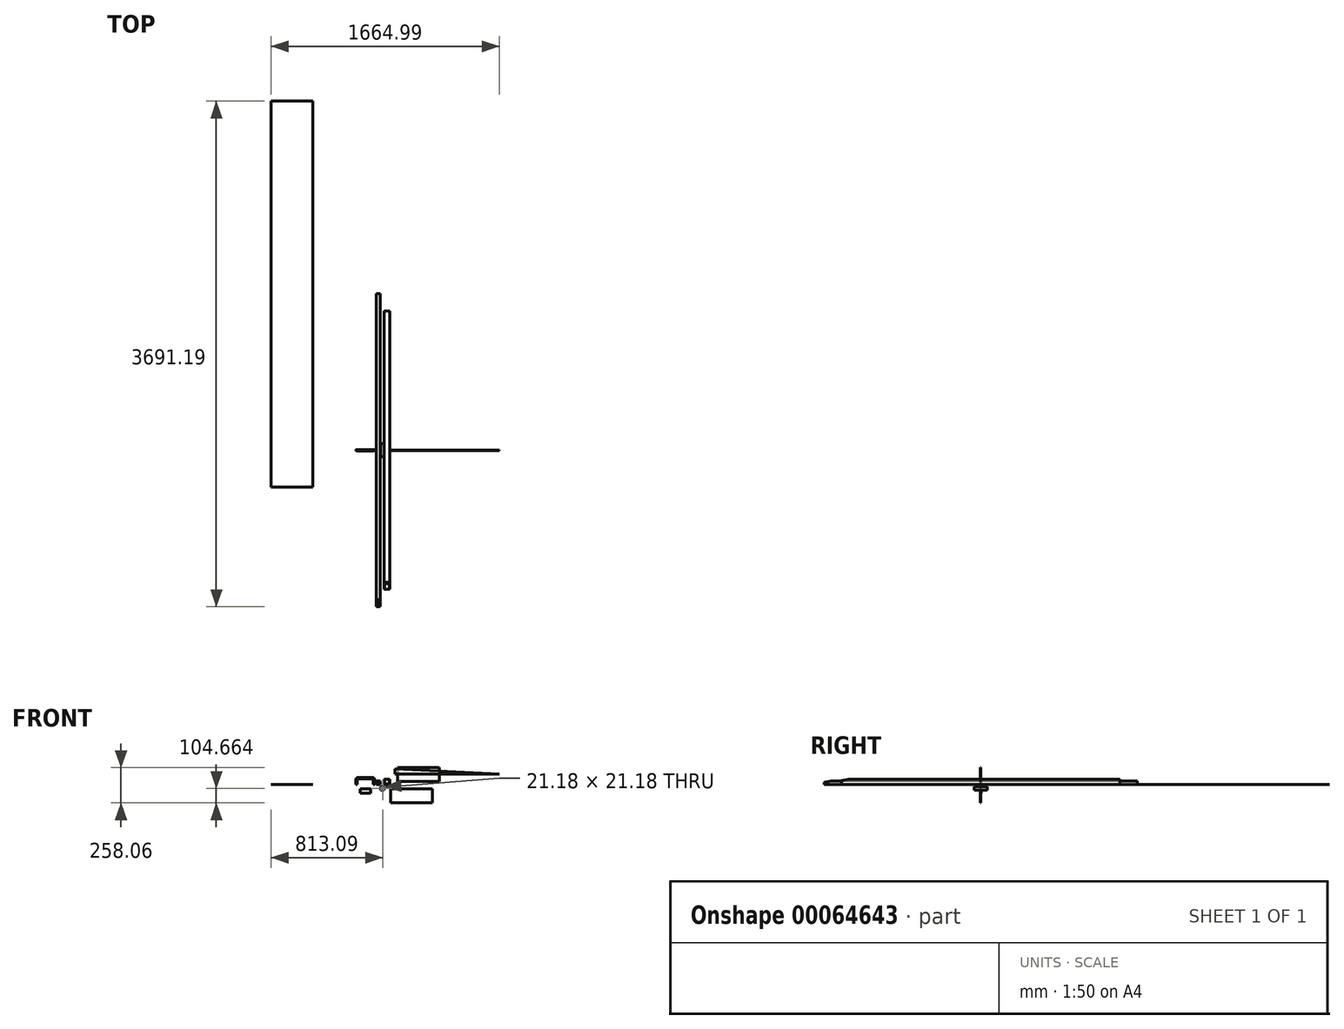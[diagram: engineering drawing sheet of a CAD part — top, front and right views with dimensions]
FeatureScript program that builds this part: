
annotation { "Feature Type Name" : "Feature", "Feature Type Description" : "" }
export const myFeature = defineFeature(function(context is Context, id is Id, definition is map)
    precondition{}
    {
        {
            var Q0;
            Q0=qCreatedBy(makeId("Front.planeOp"),FACE);
            var sketch = newSketch(context, id + "F0", { "sketchPlane" : qUnion([Q0])});
            skLineSegment(sketch, "E0.bottom", {"start": v(0, 0) * mm, "end": v(38.1, 0) * mm});
            skLineSegment(sketch, "E0.top", {"start": v(0, 38.1) * mm, "end": v(38.1, 38.1) * mm});
            skLineSegment(sketch, "E0.left", {"start": v(0, 0) * mm, "end": v(0, 38.1) * mm});
            skLineSegment(sketch, "E0.right", {"start": v(38.1, 0) * mm, "end": v(38.1, 38.1) * mm});
            skLineSegment(sketch, "E1.bottom", {"start": v(1.65, 36.45) * mm, "end": v(36.45, 36.45) * mm});
            skLineSegment(sketch, "E1.top", {"start": v(1.65, 1.65) * mm, "end": v(36.45, 1.65) * mm});
            skLineSegment(sketch, "E1.left", {"start": v(1.65, 36.45) * mm, "end": v(1.65, 1.65) * mm});
            skLineSegment(sketch, "E1.right", {"start": v(36.45, 36.45) * mm, "end": v(36.45, 1.65) * mm});
            skSolve(sketch);
        }
        {
            var Q0;
            Q0=makeQuery(id+"F0.imprint","IMPRINT",FACE,{"disambiguationData":[TD([[makeQuery(id+"F0.imprint","IMPRINT",EDGE,{"derivedFrom":sQuery(id+"F0.wireOp",EDGE,"E0.bottom")}),1.0]])]});
            extrude(context, id + "F1", {"entities" : qUnion([Q0]), "endBound" : BoundingType.SYMMETRIC, "depth" : 2032 * mm});
        }
        {
            var Q0;
            Q0=qCreatedBy(makeId("Front.planeOp"),FACE);
            var sketch = newSketch(context, id + "F2", { "sketchPlane" : qUnion([Q0])});
            skLineSegment(sketch, "E2.bottom", {"start": v(-31.74, 0) * mm, "end": v(-57.14, 0) * mm});
            skLineSegment(sketch, "E2.top", {"start": v(-31.74, 25.4) * mm, "end": v(-57.14, 25.4) * mm});
            skLineSegment(sketch, "E2.left", {"start": v(-31.74, 0) * mm, "end": v(-31.74, 25.4) * mm});
            skLineSegment(sketch, "E2.right", {"start": v(-57.14, 0) * mm, "end": v(-57.14, 25.4) * mm});
            skLineSegment(sketch, "E3.bottom", {"start": v(-55.03, 23.3) * mm, "end": v(-33.85, 23.3) * mm});
            skLineSegment(sketch, "E3.top", {"start": v(-55.03, 2.1) * mm, "end": v(-33.85, 2.1) * mm});
            skLineSegment(sketch, "E3.left", {"start": v(-55.03, 23.3) * mm, "end": v(-55.03, 2.1) * mm});
            skLineSegment(sketch, "E3.right", {"start": v(-33.85, 23.3) * mm, "end": v(-33.85, 2.1) * mm});
            skSolve(sketch);
        }
        {
            var Q0;
            Q0=makeQuery(id+"F2.imprint","IMPRINT",FACE,{"disambiguationData":[TD([[makeQuery(id+"F2.imprint","IMPRINT",EDGE,{"derivedFrom":sQuery(id+"F2.wireOp",EDGE,"E2.bottom")}),-1.0]])]});
            extrude(context, id + "F3", {"entities" : qUnion([Q0]), "endBound" : BoundingType.SYMMETRIC, "depth" : 2286 * mm});
        }
        {
            var Q0;
            Q0=qCreatedBy(makeId("Front.planeOp"),FACE);
            var sketch = newSketch(context, id + "F4", { "sketchPlane" : qUnion([Q0])});
            skLineSegment(sketch, "E4.bottom", {"start": v(-25.4, -17.9) * mm, "end": v(0, -17.9) * mm});
            skLineSegment(sketch, "E4.top", {"start": v(-25.4, -43.3) * mm, "end": v(0, -43.3) * mm});
            skLineSegment(sketch, "E4.left", {"start": v(-25.4, -17.9) * mm, "end": v(-25.4, -43.3) * mm});
            skLineSegment(sketch, "E4.right", {"start": v(0, -17.9) * mm, "end": v(0, -43.3) * mm});
            skLineSegment(sketch, "E5.bottom", {"start": v(-23.3, -20.01) * mm, "end": v(-2.1, -20.01) * mm});
            skLineSegment(sketch, "E5.top", {"start": v(-23.3, -41.2) * mm, "end": v(-2.1, -41.2) * mm});
            skLineSegment(sketch, "E5.left", {"start": v(-23.3, -20.01) * mm, "end": v(-23.3, -41.2) * mm});
            skLineSegment(sketch, "E5.right", {"start": v(-2.1, -20.01) * mm, "end": v(-2.1, -41.2) * mm});
            skSolve(sketch);
        }
        {
            var Q0;
            Q0=makeQuery(id+"F4.imprint","IMPRINT",FACE,{"disambiguationData":[TD([[makeQuery(id+"F4.imprint","IMPRINT",EDGE,{"derivedFrom":sQuery(id+"F4.wireOp",EDGE,"E4.bottom")}),-1.0]])]});
            extrude(context, id + "F5", {"entities" : qUnion([Q0]), "endBound" : BoundingType.SYMMETRIC, "depth" : 95.25 * mm});
        }
        {
            var Q0;
            Q0=qCreatedBy(makeId("Front.planeOp"),FACE);
            var sketch = newSketch(context, id + "F6", { "sketchPlane" : qUnion([Q0])});
            skLineSegment(sketch, "E6.bottom", {"start": v(45.4, -33.67) * mm, "end": v(350.2, -33.67) * mm});
            skLineSegment(sketch, "E6.top", {"start": v(45.4, -135.27) * mm, "end": v(350.2, -135.27) * mm});
            skLineSegment(sketch, "E6.left", {"start": v(45.4, -33.67) * mm, "end": v(45.4, -135.27) * mm});
            skLineSegment(sketch, "E6.right", {"start": v(350.2, -33.67) * mm, "end": v(350.2, -135.27) * mm});
            skSolve(sketch);
        }
        {
            var Q0;
            Q0=makeQuery(id+"F6.imprint","IMPRINT",FACE,{"disambiguationData":[TD([[makeQuery(id+"F6.imprint","IMPRINT",EDGE,{"derivedFrom":sQuery(id+"F6.wireOp",EDGE,"E6.bottom")}),-1.0]])]});
            extrude(context, id + "F7", {"entities" : qUnion([Q0]), "endBound" : BoundingType.SYMMETRIC, "depth" : 3.17 * mm});
        }
        {
            var Q0;
            Q0=qCreatedBy(makeId("Front.planeOp"),FACE);
            var sketch = newSketch(context, id + "F8", { "sketchPlane" : qUnion([Q0])});
            skLineSegment(sketch, "E7.bottom", {"start": v(-175.7, -33.57) * mm, "end": v(-99.5, -33.57) * mm});
            skLineSegment(sketch, "E7.top", {"start": v(-175.7, -65.32) * mm, "end": v(-99.5, -65.32) * mm});
            skLineSegment(sketch, "E7.left", {"start": v(-175.7, -33.57) * mm, "end": v(-175.7, -65.32) * mm});
            skLineSegment(sketch, "E7.right", {"start": v(-99.5, -33.57) * mm, "end": v(-99.5, -65.32) * mm});
            skSolve(sketch);
        }
        {
            var Q0;
            Q0=makeQuery(id+"F8.imprint","IMPRINT",FACE,{"disambiguationData":[TD([[makeQuery(id+"F8.imprint","IMPRINT",EDGE,{"derivedFrom":sQuery(id+"F8.wireOp",EDGE,"E7.bottom")}),-1.0]])]});
            extrude(context, id + "F9", {"entities" : qUnion([Q0]), "endBound" : BoundingType.SYMMETRIC, "depth" : 6.35 * mm});
        }
        {
            var Q0;
            Q0=qCreatedBy(makeId("Front.planeOp"),FACE);
            var sketch = newSketch(context, id + "F10", { "sketchPlane" : qUnion([Q0])});
            skLineSegment(sketch, "E8", {"start": v(-203.2, 0) * mm, "end": v(-203.2, 34.92) * mm});
            skLineSegment(sketch, "E9", {"start": v(-193.68, 44.45) * mm, "end": v(-85.73, 44.45) * mm});
            skLineSegment(sketch, "E10", {"start": v(-76.2, 34.92) * mm, "end": v(-76.2, 0) * mm});
            skPoint(sketch, "E11.visualSharp", {"position": v(-203.2, 44.45) * mm});
            skArc(sketch, "E11.filletArc", {"start": v(-193.68, 44.45) * mm, "mid": v(-200.41, 41.66) * mm, "end": v(-203.2, 34.92) * mm});
            skPoint(sketch, "E12.visualSharp", {"position": v(-76.2, 44.45) * mm});
            skArc(sketch, "E12.filletArc", {"start": v(-76.2, 34.92) * mm, "mid": v(-78.99, 41.66) * mm, "end": v(-85.73, 44.45) * mm});
            skSolve(sketch);
        }
        {
            var Q0;
            Q0=qCreatedBy(makeId("Top.planeOp"),FACE);
            var sketch = newSketch(context, id + "F11", { "sketchPlane" : qUnion([Q0])});
            skCircle(sketch, "E13", {"center": v(-76.2, 0) * mm, "radius": 4.76 * mm});
            skSolve(sketch);
        }
        {
            var Q0;
            Q0 = qSketchRegion(id + "F11", true);
            var Q1;
            Q1 = qConstructionFilter(qBodyType(qCreatedBy(id + "F10" ,EDGE), BodyType.WIRE), ConstructionObject.NO);
            sweep(context, id + "F12", {"profiles" : qUnion([Q0]), "path" : qUnion([Q1])});
        }
        {
            var Q0;
            Q0=qCreatedBy(makeId("Front.planeOp"),FACE);
            var sketch = newSketch(context, id + "F13", { "sketchPlane" : qUnion([Q0])});
            skLineSegment(sketch, "E14.bottom", {"start": v(95.73, 122.8) * mm, "end": v(400.53, 122.8) * mm});
            skLineSegment(sketch, "E14.top", {"start": v(95.73, 21.2) * mm, "end": v(400.53, 21.2) * mm});
            skLineSegment(sketch, "E14.left", {"start": v(95.73, 122.8) * mm, "end": v(95.73, 21.2) * mm});
            skLineSegment(sketch, "E14.right", {"start": v(400.53, 122.8) * mm, "end": v(400.53, 21.2) * mm});
            skSolve(sketch);
        }
        {
            var Q0;
            Q0=makeQuery(id+"F13.imprint","IMPRINT",FACE,{"disambiguationData":[TD([[makeQuery(id+"F13.imprint","IMPRINT",EDGE,{"derivedFrom":sQuery(id+"F13.wireOp",EDGE,"E14.bottom")}),-1.0]])]});
            extrude(context, id + "F14", {"entities" : qUnion([Q0]), "endBound" : BoundingType.SYMMETRIC, "depth" : 1.59 * mm});
        }
        {
            var Q0;
            Q0=qCreatedBy(makeId("Top.planeOp"),FACE);
            var sketch = newSketch(context, id + "F15", { "sketchPlane" : qUnion([Q0])});
            skLineSegment(sketch, "E15.bottom", {"start": v(-825.8, 2548.19) * mm, "end": v(-521, 2548.19) * mm});
            skLineSegment(sketch, "E15.top", {"start": v(-825.8, -271.21) * mm, "end": v(-521, -271.21) * mm});
            skLineSegment(sketch, "E15.left", {"start": v(-825.8, 2548.19) * mm, "end": v(-825.8, -271.21) * mm});
            skLineSegment(sketch, "E15.right", {"start": v(-521, 2548.19) * mm, "end": v(-521, -271.21) * mm});
            skSolve(sketch);
        }
        {
            var Q0;
            Q0=makeQuery(id+"F15.imprint","IMPRINT",FACE,{"disambiguationData":[TD([[makeQuery(id+"F15.imprint","IMPRINT",EDGE,{"derivedFrom":sQuery(id+"F15.wireOp",EDGE,"E15.bottom")}),-1.0]])]});
            extrude(context, id + "F16", {"entities" : qUnion([Q0]), "endBound" : BoundingType.SYMMETRIC, "depth" : 1.78 * mm});
        }
        {
            var Q0;
            Q0=makeQuery(id+"F1.opExtrude","SWEPT_FACE",FACE,{"disambiguationData":[OSD([sQuery(id+"F0.wireOp",EDGE,"E0.right")])]});
            var sketch = newSketch(context, id + "F17", { "sketchPlane" : qUnion([Q0])});
            skLineSegment(sketch, "E16", {"start": v(-1016, 38.1) * mm, "end": v(-1016, 29.14) * mm});
            skLineSegment(sketch, "E17", {"start": v(-1016, 29.14) * mm, "end": v(-965.2, 38.1) * mm});
            skLineSegment(sketch, "E18", {"start": v(-965.2, 38.1) * mm, "end": v(-1016, 38.1) * mm});
            skSolve(sketch);
        }
        {
            var Q0;
            Q0=makeQuery(id+"F17.imprint","IMPRINT",FACE,{"disambiguationData":[TD([[makeQuery(id+"F17.imprint","IMPRINT",EDGE,{"derivedFrom":sQuery(id+"F17.wireOp",EDGE,"E16")}),-1.0]])]});
            var Q1;
            Q1=makeQuery(id+"F1.opExtrude","SWEPT_FACE",FACE,{"disambiguationData":[OSD([sQuery(id+"F0.wireOp",EDGE,"E0.left")])]});
            extrude(context, id + "F18", {"entities" : qUnion([Q0]), "operationType" : NewBodyOperationType.REMOVE, "endBound" : BoundingType.UP_TO_SURFACE, "oppositeDirection" : true, "endBoundEntityFace" : qUnion([Q1]), "depth" : 25.4 * mm});
        }
        {
            var Q0;
            Q0=makeQuery(id+"F3.opExtrude","SWEPT_FACE",FACE,{"disambiguationData":[OSD([sQuery(id+"F2.wireOp",EDGE,"E2.left")])]});
            var sketch = newSketch(context, id + "F19", { "sketchPlane" : qUnion([Q0])});
            skLineSegment(sketch, "E19", {"start": v(-1143, 25.4) * mm, "end": v(-1143, 16.44) * mm});
            skLineSegment(sketch, "E20", {"start": v(-1143, 16.44) * mm, "end": v(-1092.2, 25.4) * mm});
            skLineSegment(sketch, "E21", {"start": v(-1092.2, 25.4) * mm, "end": v(-1143, 25.4) * mm});
            skSolve(sketch);
        }
        {
            var Q0;
            Q0=makeQuery(id+"F19.imprint","IMPRINT",FACE,{"disambiguationData":[TD([[makeQuery(id+"F19.imprint","IMPRINT",EDGE,{"derivedFrom":sQuery(id+"F19.wireOp",EDGE,"E19")}),-1.0]])]});
            var Q1;
            Q1=makeQuery(id+"F3.opExtrude","SWEPT_FACE",FACE,{"disambiguationData":[OSD([sQuery(id+"F2.wireOp",EDGE,"E2.right")])]});
            extrude(context, id + "F20", {"entities" : qUnion([Q0]), "operationType" : NewBodyOperationType.REMOVE, "endBound" : BoundingType.UP_TO_SURFACE, "oppositeDirection" : true, "endBoundEntityFace" : qUnion([Q1]), "depth" : 25.4 * mm});
        }
        {
            var Q0;
            Q0=qCreatedBy(makeId("Front.planeOp"),FACE);
            var sketch = newSketch(context, id + "F21", { "sketchPlane" : qUnion([Q0])});
            skLineSegment(sketch, "E22", {"start": v(77.2, 74.06) * mm, "end": v(77.2, 112.16) * mm});
            skLineSegment(sketch, "E23", {"start": v(77.2, 112.16) * mm, "end": v(839.2, 74.06) * mm});
            skLineSegment(sketch, "E24", {"start": v(839.2, 74.06) * mm, "end": v(77.2, 74.06) * mm});
            skSolve(sketch);
        }
        {
            var Q0;
            Q0=makeQuery(id+"F21.imprint","IMPRINT",FACE,{"disambiguationData":[TD([[makeQuery(id+"F21.imprint","IMPRINT",EDGE,{"derivedFrom":sQuery(id+"F21.wireOp",EDGE,"E22")}),-1.0]])]});
            extrude(context, id + "F22", {"entities" : qUnion([Q0]), "endBound" : BoundingType.SYMMETRIC, "depth" : 3.17 * mm});
        }
    });
